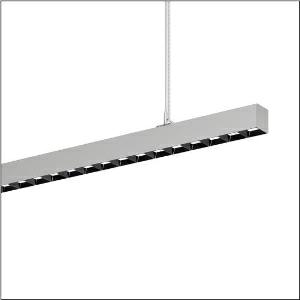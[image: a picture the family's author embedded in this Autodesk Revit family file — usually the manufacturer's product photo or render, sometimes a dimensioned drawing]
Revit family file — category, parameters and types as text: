
# Revit family: silica_21_51mx31tctds
name_source: partatom
category: Lighting Fixtures
units: mm (PartAtom-declared; Revit-internal decimal feet)

## family parameters
Cut with Voids When Loaded = No
Host = Face
Light Source = No
Part Type = Normal
Room Calculation Point = No
Round Connector Dimension = Use Diameter
Shared = No

## types (1)
- --- (1 x LED, 15550 lm, 133.9 W, 6500K)
    Apparent Load = 134 VA
    CIE Flux Codes = 85 99 100 60 100
    Color Rendering = 80
    Color Temperature = 6500K
    Default Elevation = 1800 mm
    Description = Silica 21, office luminaire, primary light control with darklight reflector, of PMMA, black, CAT 2 (L<= 3000cd/m²), light emission: direct/indirect distribution, primary light characteristic: symmetric, installation type: suspended mounting, LED, rated luminous flux: 15.550lm, luminous efficacy: 111lm/W, light colour: 8tw, colour temperature: 2700..6500K, control gear: DALI DT8, with terminal, 3+2-pole, max. 2.5mm², mains connection: 220..240V, AC, 50/60Hz, rated input power: 140.6W, luminaire housing, of aluminium, metallic grey (RAL 9006), length: 3.004mm, width: 53mm, height: 53mm, protection rating (complete): IP20, insulation class (complete): insulation class I (protective earthing), certification: CE, permissible operating ambient temperature: 0..+35°C, standard: EN 50419, packaging unit: 1 piece
    Height = 53 mm
    Lamp = 1 x LED
    Lamp Light Flux = 15550 lm
    Lamp Power = 133.9 W
    Lamp count = 1
    Length = 3004 mm
    Luminous efficacy = 116 lm/W
    Manufacturer = Siteco
    ModVariant = No
    Model = 51MX31TCTDS
    Mounting Place = Ceiling
    Mounting Type = Pendant
    Number of Poles = 1
    OnlyDefault = Yes
    Power Factor = 1
    Product Name = Silica 21
    Product group = office luminaire | ceiling pendant
    ProductGroupID = 903
    Protection Class = Protection class I
    Protection Degree = IP 20
    RLX_Detail_Level = 1
    RLX_Emergency_Light_Flux = 0 lm
    RLX_Emergency_Type = 0
    RLX_Emergency_Type_DB = No
    RlxData = <blob elided: 62537 chars, md5=aca28334>
    Socket = socket
    Standby Power = 0 W
    System Light Flux = 15550 lm
    System Power = 134 W
    Type Comments = individual setting
    Type Image = l_1335859.jpg
    URL = http://relux.com
    VarID = @adj_140911
    Voltage = 0 V
    Weight = 0.00 kg
    Width = 53 mm

## geometry (parser evidence)
native form markers: Blend x4, Sweep x11
no freeform markers — native parametric forms only
